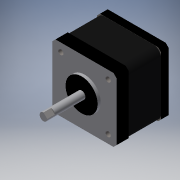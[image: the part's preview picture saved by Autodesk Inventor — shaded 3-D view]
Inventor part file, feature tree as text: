
AUTODESK INVENTOR PART (.ipt)
format: ipt  version: 2017 (Build 210142000, 142)  size: 172,032 bytes
history: native  units: in
note: dims shown in document units (in); Inventor stores cm internally (conversion verified against a paired STEP export)
features: other x2, extrude x1, imported_body x1, sketch x1
ambient origin geometry x8: Origin, YZ Plane, XZ Plane, XY Plane, X Axis, Y Axis, Z Axis, Center Point
bodies: Body1 (feature_tree)
feature tree (5):
  other  "Cut-Extrude6"
  other  "stepper (hardware)1"
  extrude  "Extrusion1"  [1 undecoded]
  imported_body  "Base1"
  sketch  "Sketch2"  dims[d0=0.1969in d1=0.0in]
note: 1 required parameter value undecoded (feature->parameter linkage not recoverable at this tier; creation-order binding heuristic only, values carry confidence <= 0.55)
